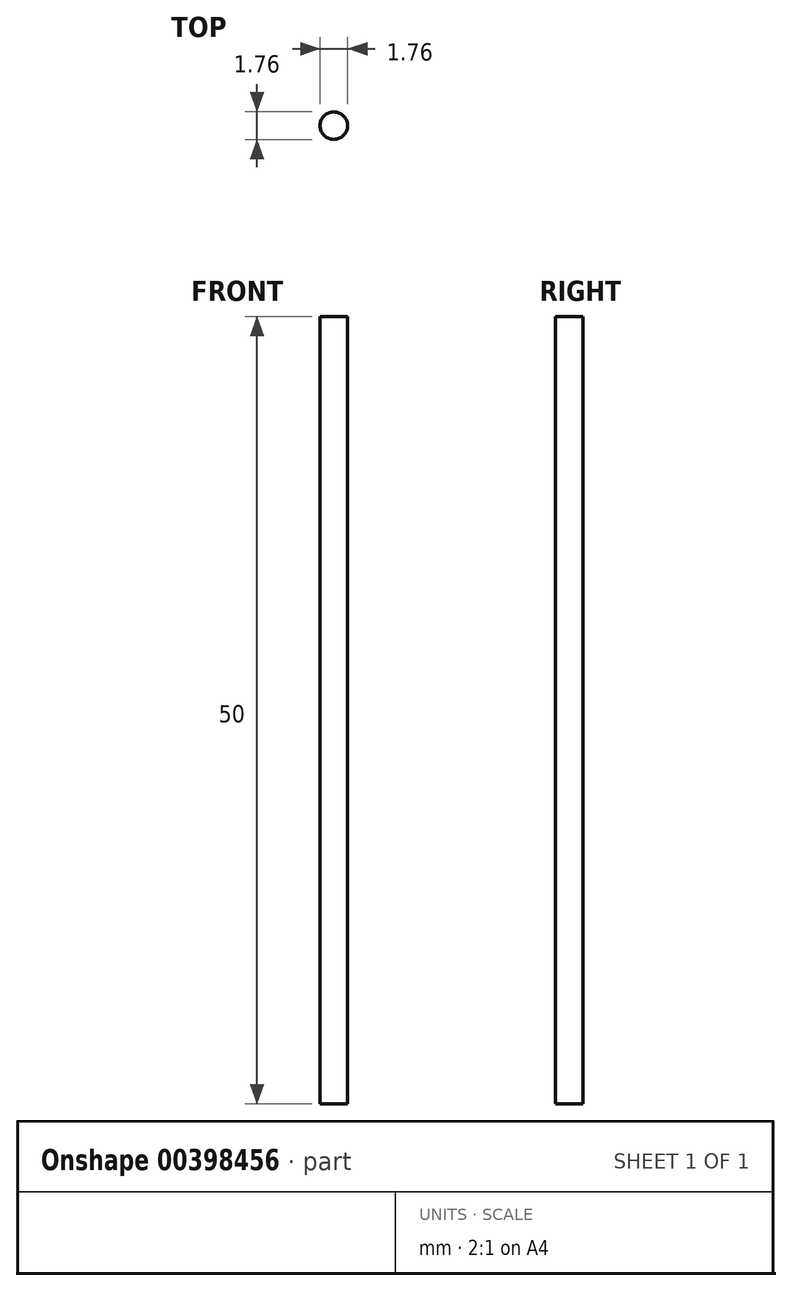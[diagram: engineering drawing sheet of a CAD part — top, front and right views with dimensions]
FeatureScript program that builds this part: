
annotation { "Feature Type Name" : "Feature", "Feature Type Description" : "" }
export const myFeature = defineFeature(function(context is Context, id is Id, definition is map)
    precondition{}
    {
        {
            var Q0;
            Q0=qCreatedBy(makeId("Top.planeOp"),FACE);
            var sketch = newSketch(context, id + "F0", { "sketchPlane" : qUnion([Q0])});
            skCircle(sketch, "E0", {"center": v(0, 0) * mm, "radius": 0.88 * mm});
            skSolve(sketch);
        }
        {
            var Q0;
            Q0 = qSketchRegion(id + "F0", true);
            extrude(context, id + "F1", {"entities" : qUnion([Q0]), "depth" : 50 * mm, "offsetDistance" : 25 * mm});
        }
    });
